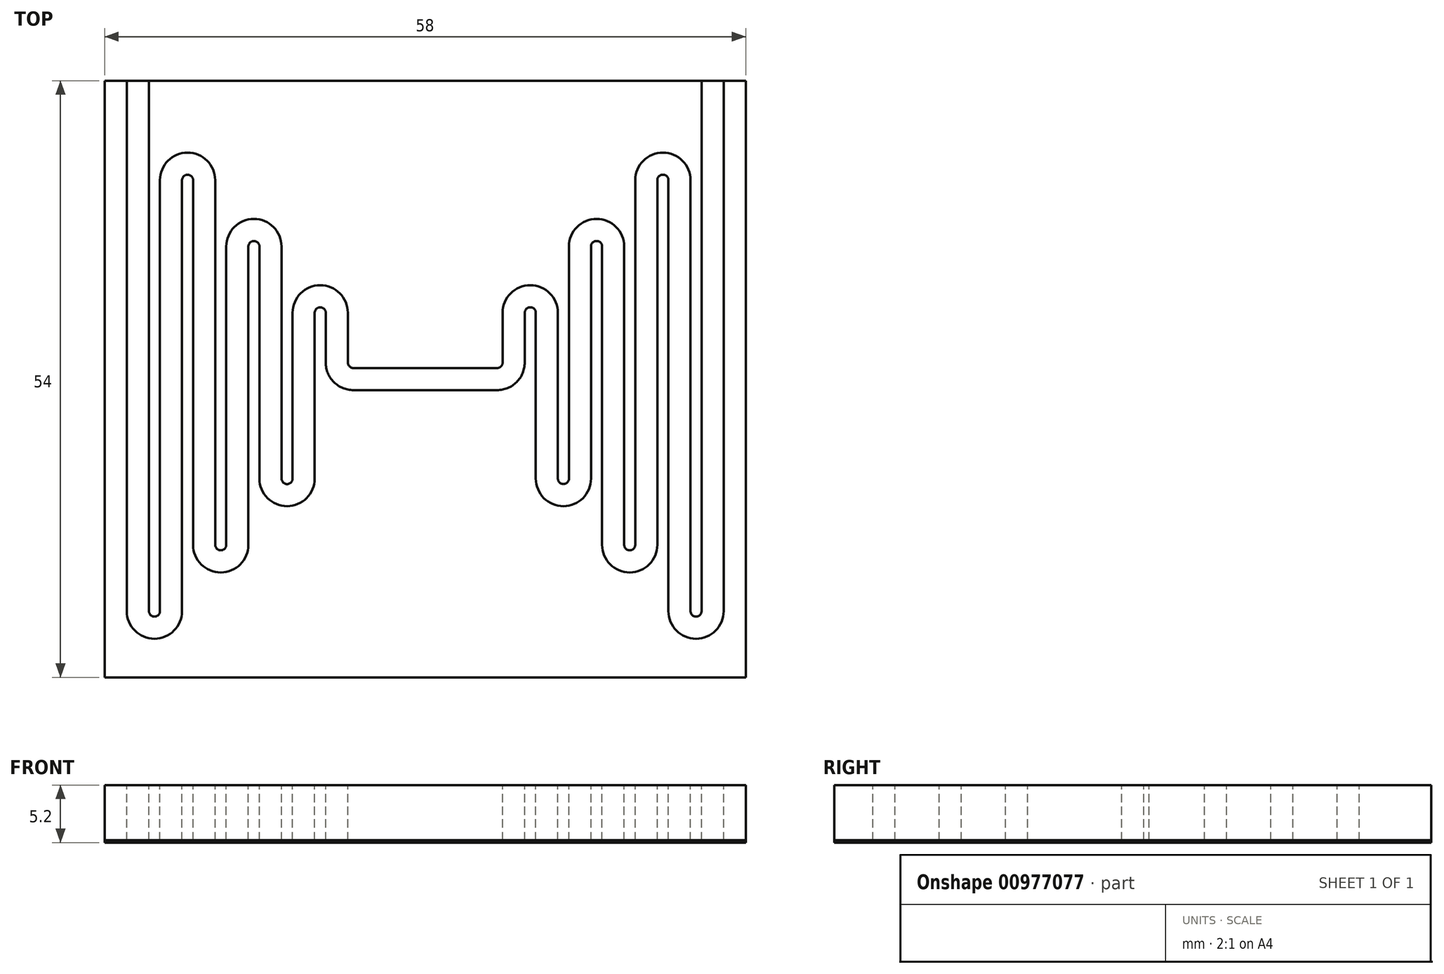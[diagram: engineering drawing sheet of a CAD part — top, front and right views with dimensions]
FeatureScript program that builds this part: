
annotation { "Feature Type Name" : "Feature", "Feature Type Description" : "" }
export const myFeature = defineFeature(function(context is Context, id is Id, definition is map)
    precondition{}
    {
        {
            var Q0;
            Q0=qCreatedBy(makeId("Front.planeOp"),FACE);
            var sketch = newSketch(context, id + "F0", { "sketchPlane" : qUnion([Q0])});
            skLineSegment(sketch, "E0.bottom", {"start": v(29, 2.5) * mm, "end": v(-29, 2.5) * mm});
            skLineSegment(sketch, "E0.top", {"start": v(29, -2.5) * mm, "end": v(-29, -2.5) * mm});
            skLineSegment(sketch, "E0.left", {"start": v(29, 2.5) * mm, "end": v(29, -2.5) * mm});
            skLineSegment(sketch, "E0.right", {"start": v(-29, 2.5) * mm, "end": v(-29, -2.5) * mm});
            skPoint(sketch, "E0.middle", {"position": v(0, 0) * mm});
            skSolve(sketch);
        }
        {
            var Q0;
            Q0=makeQuery(id+"F0.imprint","IMPRINT",FACE,{"disambiguationData":[TD([[makeQuery(id+"F0.imprint","IMPRINT",EDGE,{"derivedFrom":sQuery(id+"F0.wireOp",EDGE,"E0.bottom")}),1.0]])]});
            extrude(context, id + "F1", {"entities" : qUnion([Q0]), "endBound" : BoundingType.SYMMETRIC, "depth" : 54 * mm, "offsetDistance" : 25 * mm});
        }
        {
            var Q0;
            Q0=qCreatedBy(makeId("Top.planeOp"),FACE);
            var sketch = newSketch(context, id + "F2", { "sketchPlane" : qUnion([Q0])});
            skPoint(sketch, "E1.middle", {"position": v(-28, 0) * mm});
            skLineSegment(sketch, "E2.left", {"start": v(-27, 25) * mm, "end": v(-27, -21) * mm});
            skLineSegment(sketch, "E2.right", {"start": v(-25, 25) * mm, "end": v(-25, -21) * mm});
            skLineSegment(sketch, "E3.left", {"start": v(-25, 18) * mm, "end": v(-25, -21) * mm});
            skLineSegment(sketch, "E3.right", {"start": v(-24, 18) * mm, "end": v(-24, -21) * mm});
            skLineSegment(sketch, "E4.right", {"start": v(-22, 18) * mm, "end": v(-22, -21) * mm});
            skLineSegment(sketch, "E5.left", {"start": v(-21, 18) * mm, "end": v(-21, -15) * mm});
            skLineSegment(sketch, "E5.right", {"start": v(-19, 18) * mm, "end": v(-19, -15) * mm});
            skLineSegment(sketch, "E6.left", {"start": v(-18, 12) * mm, "end": v(-18, -15) * mm});
            skLineSegment(sketch, "E6.right", {"start": v(-16, 12) * mm, "end": v(-16, -15) * mm});
            skLineSegment(sketch, "E7.left", {"start": v(-15, 12) * mm, "end": v(-15, -9) * mm});
            skLineSegment(sketch, "E7.right", {"start": v(-13, 12) * mm, "end": v(-13, -9) * mm});
            skLineSegment(sketch, "E8.left", {"start": v(-12, 6) * mm, "end": v(-12, -9) * mm});
            skLineSegment(sketch, "E8.right", {"start": v(-10, 6) * mm, "end": v(-10, -9) * mm});
            skPoint(sketch, "E9.firstSnap0", {"position": v(-13, 1.5) * mm});
            skLineSegment(sketch, "E10.left", {"start": v(-9, 6) * mm, "end": v(-9, 1.5) * mm});
            skLineSegment(sketch, "E10.right", {"start": v(-7, 6) * mm, "end": v(-7, 1.5) * mm});
            skLineSegment(sketch, "E11.bottom", {"start": v(6.5, 1) * mm, "end": v(-6.5, 1) * mm});
            skLineSegment(sketch, "E11.top", {"start": v(6.5, -1) * mm, "end": v(-6.5, -1) * mm});
            skPoint(sketch, "E11.middle", {"position": v(0, 0) * mm});
            skArc(sketch, "E12", {"start": v(-9, 6) * mm, "mid": v(-9.5, 6.5) * mm, "end": v(-10, 6) * mm});
            skArc(sketch, "E13", {"start": v(-7, 6) * mm, "mid": v(-9.5, 8.5) * mm, "end": v(-12, 6) * mm});
            skArc(sketch, "E14", {"start": v(-13, -9) * mm, "mid": v(-12.5, -9.5) * mm, "end": v(-12, -9) * mm});
            skArc(sketch, "E15", {"start": v(-15, -9) * mm, "mid": v(-12.5, -11.5) * mm, "end": v(-10, -9) * mm});
            skArc(sketch, "E16", {"start": v(-15, 12) * mm, "mid": v(-15.5, 12.5) * mm, "end": v(-16, 12) * mm});
            skArc(sketch, "E17", {"start": v(-13, 12) * mm, "mid": v(-15.5, 14.5) * mm, "end": v(-18, 12) * mm});
            skArc(sketch, "E18", {"start": v(-19, -15) * mm, "mid": v(-18.5, -15.5) * mm, "end": v(-18, -15) * mm});
            skArc(sketch, "E19", {"start": v(-21, -15) * mm, "mid": v(-18.5, -17.5) * mm, "end": v(-16, -15) * mm});
            skArc(sketch, "E20", {"start": v(-21, 18) * mm, "mid": v(-21.5, 18.5) * mm, "end": v(-22, 18) * mm});
            skArc(sketch, "E21", {"start": v(-19, 18) * mm, "mid": v(-21.5, 20.5) * mm, "end": v(-24, 18) * mm});
            skArc(sketch, "E22", {"start": v(-25, -21) * mm, "mid": v(-24.5, -21.5) * mm, "end": v(-24, -21) * mm});
            skArc(sketch, "E23", {"start": v(-27, -21) * mm, "mid": v(-24.5, -23.5) * mm, "end": v(-22, -21) * mm});
            skArc(sketch, "E24", {"start": v(-7, 1.5) * mm, "mid": v(-6.85, 1.15) * mm, "end": v(-6.5, 1) * mm});
            skArc(sketch, "E25", {"start": v(-9, 1.5) * mm, "mid": v(-8.27, -0.27) * mm, "end": v(-6.5, -1) * mm});
            skLineSegment(sketch, "E26.left", {"start": v(25, 25) * mm, "end": v(25, -21) * mm});
            skLineSegment(sketch, "E26.right", {"start": v(27, 25) * mm, "end": v(27, -21) * mm});
            skLineSegment(sketch, "E27.left", {"start": v(22, 18) * mm, "end": v(22, -21) * mm});
            skLineSegment(sketch, "E27.right", {"start": v(24, 18) * mm, "end": v(24, -21) * mm});
            skLineSegment(sketch, "E28.left", {"start": v(19, 18) * mm, "end": v(19, -15) * mm});
            skLineSegment(sketch, "E28.right", {"start": v(21, 18) * mm, "end": v(21, -15) * mm});
            skLineSegment(sketch, "E29.left", {"start": v(16, 12) * mm, "end": v(16, -15) * mm});
            skLineSegment(sketch, "E29.right", {"start": v(18, 12) * mm, "end": v(18, -15) * mm});
            skLineSegment(sketch, "E30.left", {"start": v(13, 12) * mm, "end": v(13, -9) * mm});
            skLineSegment(sketch, "E30.right", {"start": v(15, 12) * mm, "end": v(15, -9) * mm});
            skLineSegment(sketch, "E31.left", {"start": v(10, 6) * mm, "end": v(10, -9) * mm});
            skLineSegment(sketch, "E31.right", {"start": v(12, 6) * mm, "end": v(12, -9) * mm});
            skLineSegment(sketch, "E32.left", {"start": v(7, 6) * mm, "end": v(7, 1.5) * mm});
            skLineSegment(sketch, "E32.right", {"start": v(9, 6) * mm, "end": v(9, 1.5) * mm});
            skArc(sketch, "E33", {"start": v(6.5, 1) * mm, "mid": v(6.85, 1.15) * mm, "end": v(7, 1.5) * mm});
            skArc(sketch, "E34", {"start": v(6.5, -1) * mm, "mid": v(8.27, -0.27) * mm, "end": v(9, 1.5) * mm});
            skArc(sketch, "E35", {"start": v(22, -21) * mm, "mid": v(24.5, -23.5) * mm, "end": v(27, -21) * mm});
            skArc(sketch, "E36", {"start": v(24, -21) * mm, "mid": v(24.5, -21.5) * mm, "end": v(25, -21) * mm});
            skArc(sketch, "E37", {"start": v(18, -15) * mm, "mid": v(18.5, -15.5) * mm, "end": v(19, -15) * mm});
            skArc(sketch, "E38", {"start": v(16, -15) * mm, "mid": v(18.5, -17.5) * mm, "end": v(21, -15) * mm});
            skArc(sketch, "E39", {"start": v(12, -9) * mm, "mid": v(12.5, -9.5) * mm, "end": v(13, -9) * mm});
            skArc(sketch, "E40", {"start": v(10, -9) * mm, "mid": v(12.5, -11.5) * mm, "end": v(15, -9) * mm});
            skArc(sketch, "E41", {"start": v(22, 18) * mm, "mid": v(21.5, 18.5) * mm, "end": v(21, 18) * mm});
            skArc(sketch, "E42", {"start": v(24, 18) * mm, "mid": v(21.5, 20.5) * mm, "end": v(19, 18) * mm});
            skArc(sketch, "E43", {"start": v(16, 12) * mm, "mid": v(15.5, 12.5) * mm, "end": v(15, 12) * mm});
            skArc(sketch, "E44", {"start": v(18, 12) * mm, "mid": v(15.5, 14.5) * mm, "end": v(13, 12) * mm});
            skArc(sketch, "E45", {"start": v(10, 6) * mm, "mid": v(9.5, 6.5) * mm, "end": v(9, 6) * mm});
            skArc(sketch, "E46", {"start": v(12, 6) * mm, "mid": v(9.5, 8.5) * mm, "end": v(7, 6) * mm});
            skLineSegment(sketch, "E47.top", {"start": v(-27, 27) * mm, "end": v(-25, 27) * mm});
            skLineSegment(sketch, "E47.left", {"start": v(-27, 25) * mm, "end": v(-27, 27) * mm});
            skLineSegment(sketch, "E47.right", {"start": v(-25, 25) * mm, "end": v(-25, 27) * mm});
            skLineSegment(sketch, "E48.top", {"start": v(25, 27) * mm, "end": v(27, 27) * mm});
            skLineSegment(sketch, "E48.left", {"start": v(25, 25) * mm, "end": v(25, 27) * mm});
            skLineSegment(sketch, "E48.right", {"start": v(27, 25) * mm, "end": v(27, 27) * mm});
            skSolve(sketch);
        }
        {
            var Q0;
            Q0 = qSketchRegion(id + "F2", true);
            extrude(context, id + "F3", {"entities" : qUnion([Q0]), "operationType" : NewBodyOperationType.REMOVE, "endBound" : BoundingType.SYMMETRIC, "oppositeDirection" : true, "depth" : 10 * mm, "offsetDistance" : 25 * mm});
        }
        {
            var Q0;
            {var subQ1=sQuery(id+"F0.wireOp",EDGE,"E0.left");var subQ2=sQuery(id+"F0.wireOp",EDGE,"E0.top");Q0=makeQuery(id+"F3.boolean.opBoolean","SPLIT",FACE,{"disambiguationData":[TD([makeQuery(id+"F1.opExtrude","SWEPT_FACE",FACE,{"disambiguationData":[OSD([subQ1])]})])],"derivedFrom":makeQuery(id+"F1.opExtrude","SWEPT_FACE",FACE,{"disambiguationData":[OSD([subQ2])]})});}
            var sketch = newSketch(context, id + "F4", { "sketchPlane" : qUnion([Q0])});
            skLineSegment(sketch, "E49.bottom", {"start": v(-29, 27) * mm, "end": v(29, 27) * mm});
            skLineSegment(sketch, "E49.top", {"start": v(-29, -27) * mm, "end": v(29, -27) * mm});
            skLineSegment(sketch, "E49.left", {"start": v(-29, 27) * mm, "end": v(-29, -27) * mm});
            skLineSegment(sketch, "E49.right", {"start": v(29, 27) * mm, "end": v(29, -27) * mm});
            skSolve(sketch);
        }
        {
            var Q0;
            Q0 = qSketchRegion(id + "F4", true);
            extrude(context, id + "F5", {"entities" : qUnion([Q0]), "depth" : 0.2 * mm, "offsetDistance" : 25 * mm});
        }
    });
